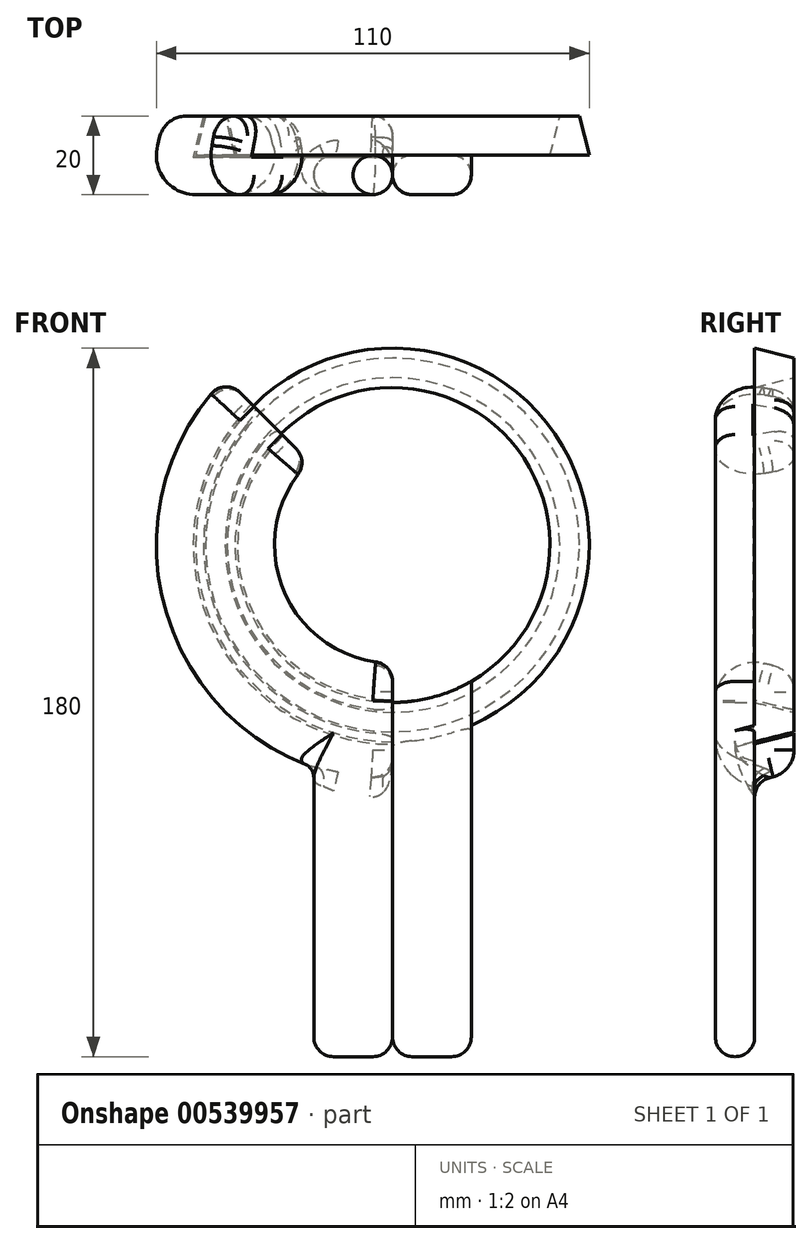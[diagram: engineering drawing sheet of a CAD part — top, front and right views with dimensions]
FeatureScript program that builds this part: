
annotation { "Feature Type Name" : "Feature", "Feature Type Description" : "" }
export const myFeature = defineFeature(function(context is Context, id is Id, definition is map)
    precondition{}
    {
        {
            var Q0;
            Q0=qCreatedBy(makeId("Right.planeOp"),FACE);
            var sketch = newSketch(context, id + "F0", { "sketchPlane" : qUnion([Q0])});
            skLineSegment(sketch, "E0", {"start": v(0, 50) * mm, "end": v(0, 40) * mm});
            skLineSegment(sketch, "E1", {"start": v(0, 40) * mm, "end": v(10, 42.5) * mm});
            skLineSegment(sketch, "E2", {"start": v(10, 42.5) * mm, "end": v(10, 47.5) * mm});
            skLineSegment(sketch, "E3", {"start": v(10, 47.5) * mm, "end": v(0, 50) * mm});
            skPoint(sketch, "E4", {"position": v(0, 45) * mm});
            skPoint(sketch, "E5", {"position": v(10, 45) * mm});
            skLineSegment(sketch, "E6", {"start": v(0, 0) * mm, "end": v(10, 0) * mm});
            skSolve(sketch);
        }
        {
            var Q0;
            Q0 = qSketchRegion(id + "F0", true);
            var Q1;
            Q1=sQuery(id+"F0.wireOp",EDGE,"E6");
            revolve(context, id + "F1", {"entities" : qUnion([Q0]), "axis" : qUnion([Q1]), "revolveType" : RevolveType.FULL});
        }
        {
            var Q0;
            Q0=qCreatedBy(makeId("Front.planeOp"),FACE);
            var sketch = newSketch(context, id + "F2", { "sketchPlane" : qUnion([Q0])});
            skLineSegment(sketch, "E7", {"start": v(0, -40) * mm, "end": v(0, -130) * mm});
            skLineSegment(sketch, "E8", {"start": v(0, -130) * mm, "end": v(20, -130) * mm});
            skLineSegment(sketch, "E9", {"start": v(20, -130) * mm, "end": v(20, -34.64) * mm});
            skArc(sketch, "E10", {"start": v(0, -40) * mm, "mid": v(10.35, -38.64) * mm, "end": v(20, -34.64) * mm});
            skSolve(sketch);
        }
        {
            var Q0;
            Q0 = qSketchRegion(id + "F2", true);
            extrude(context, id + "F3", {"entities" : qUnion([Q0]), "operationType" : NewBodyOperationType.ADD, "depth" : 10 * mm, "offsetDistance" : 25 * mm});
        }
        {
            var Q0;
            Q0=qCreatedBy(makeId("Right.planeOp"),FACE);
            var sketch = newSketch(context, id + "F4", { "sketchPlane" : qUnion([Q0])});
            skLineSegment(sketch, "E11", {"start": v(0, -45) * mm, "end": v(0, -50) * mm});
            skPoint(sketch, "E12", {"position": v(0, -45) * mm});
            skPoint(sketch, "E13", {"position": v(10, -45) * mm});
            skLineSegment(sketch, "E14", {"start": v(0, 0) * mm, "end": v(10, 0) * mm});
            skLineSegment(sketch, "E15.0", {"start": v(-0.5, -50.64) * mm, "end": v(10, -48.02) * mm});
            skLineSegment(sketch, "E15.1", {"start": v(-0.5, -39.36) * mm, "end": v(-0.5, -50.64) * mm});
            skLineSegment(sketch, "E15.2", {"start": v(10, -41.98) * mm, "end": v(-0.5, -39.36) * mm});
            skLineSegment(sketch, "E16.0", {"start": v(-10, -62.8) * mm, "end": v(10, -57.8) * mm});
            skLineSegment(sketch, "E16.1", {"start": v(-10, -27.2) * mm, "end": v(-10, -62.8) * mm});
            skLineSegment(sketch, "E16.2", {"start": v(10, -32.2) * mm, "end": v(-10, -27.2) * mm});
            skLineSegment(sketch, "E17", {"start": v(10, -32.2) * mm, "end": v(10, -41.98) * mm});
            skLineSegment(sketch, "E18", {"start": v(10, -48.02) * mm, "end": v(10, -57.8) * mm});
            skPoint(sketch, "E19.end.orphan", {"position": v(10, -47.5) * mm});
            skPoint(sketch, "E20.start.orphan", {"position": v(10, -42.5) * mm});
            skPoint(sketch, "E21.orphan", {"position": v(0, -40) * mm});
            skSolve(sketch);
        }
        {
            var Q0;
            Q0 = qSketchRegion(id + "F4", true);
            var Q1;
            Q1=sQuery(id+"F0.wireOp",EDGE,"E6");
            revolve(context, id + "F5", {"entities" : qUnion([Q0]), "axis" : qUnion([Q1]), "revolveType" : RevolveType.ONE_DIRECTION, "angle" : 135 * degree});
        }
        {
            var Q0;
            Q0=makeQuery(id+"F5.opRevolve","SWEPT_FACE",FACE,{"disambiguationData":[OSD([sQuery(id+"F4.wireOp",EDGE,"E16.1")])]});
            var sketch = newSketch(context, id + "F6", { "sketchPlane" : qUnion([Q0])});
            skLineSegment(sketch, "E22", {"start": v(0, -130) * mm, "end": v(-20, -130) * mm});
            skLineSegment(sketch, "E23", {"start": v(-20, -130) * mm, "end": v(-20, -54.24) * mm});
            skArc(sketch, "E24", {"start": v(-20, -54.24) * mm, "mid": v(-10.16, -56.9) * mm, "end": v(0, -57.8) * mm});
            skLineSegment(sketch, "E25", {"start": v(0, -57.8) * mm, "end": v(0, -130) * mm});
            skSolve(sketch);
        }
        {
            var Q0;
            Q0 = qSketchRegion(id + "F6", true);
            extrude(context, id + "F7", {"entities" : qUnion([Q0]), "oppositeDirection" : true, "depth" : 10 * mm, "offsetDistance" : 25 * mm});
        }
        {
            var Q0;
            Q0=makeQuery(id+"F5.opRevolve","SWEPT_BODY",BODY,{"disambiguationData":[OSD([sQuery(id+"F4.wireOp",EDGE,"E15.0"),sQuery(id+"F4.wireOp",EDGE,"E15.1"),sQuery(id+"F4.wireOp",EDGE,"E15.2"),sQuery(id+"F4.wireOp",EDGE,"E16.0"),sQuery(id+"F4.wireOp",EDGE,"E16.1"),sQuery(id+"F4.wireOp",EDGE,"E16.2"),sQuery(id+"F4.wireOp",EDGE,"E17"),sQuery(id+"F4.wireOp",EDGE,"E18")])]});
            var Q1;
            Q1=makeQuery(id+"F7.opExtrude","SWEPT_BODY",BODY,{"disambiguationData":[OSD([sQuery(id+"F6.wireOp",EDGE,"E22"),sQuery(id+"F6.wireOp",EDGE,"E23"),sQuery(id+"F6.wireOp",EDGE,"E24"),sQuery(id+"F6.wireOp",EDGE,"E25")])]});
            booleanBodies(context, id + "F8", {"operationType" : BooleanOperationType.UNION, "tools" : qUnion([Q0, Q1])});
        }
        {
            var Q0;
            Q0=makeQuery(id+"F5.opRevolve","SWEPT_EDGE",EDGE,{"disambiguationData":[OSD([sQuery(id+"F4.wireOp",EDGE,"E16.0"),sQuery(id+"F4.wireOp",EDGE,"E18")])]});
            var Q1;
            Q1=makeQuery(id+"F5.opRevolve","SWEPT_EDGE",EDGE,{"disambiguationData":[OSD([sQuery(id+"F4.wireOp",EDGE,"E16.2"),sQuery(id+"F4.wireOp",EDGE,"E17")])]});
            fillet(context, id + "F9", {"entities" : qUnion([Q0, Q1]), "radius" : 7 * mm, "tangentPropagation" : true, "allowEdgeOverflow" : false});
        }
        {
            var Q0;
            Q0=makeQuery(id+"F5.opRevolve","SWEPT_EDGE",EDGE,{"disambiguationData":[OSD([sQuery(id+"F4.wireOp",EDGE,"E16.0"),sQuery(id+"F4.wireOp",EDGE,"E16.1")])]});
            var Q1;
            Q1=makeQuery(id+"F5.opRevolve","SWEPT_EDGE",EDGE,{"disambiguationData":[OSD([sQuery(id+"F4.wireOp",EDGE,"E16.1"),sQuery(id+"F4.wireOp",EDGE,"E16.2")])]});
            var Q2;
            Q2=makeQuery(id+"F3.opExtrude","CAP_EDGE",EDGE,{"disambiguationData":[OSD([sQuery(id+"F2.wireOp",EDGE,"E10")])],"isStart":false});
            var Q3;
            {var subQ0=sQuery(id+"F0.wireOp",EDGE,"E3");Q3=makeQuery(id+"F3.boolean.opBoolean","SPLIT",EDGE,{"disambiguationData":[topologyDisambiguationEdgeConnected([makeQuery(id+"F3.opExtrude","CAP_FACE",FACE,{"disambiguationData":[OSD([sQuery(id+"F2.wireOp",EDGE,"E7"),sQuery(id+"F2.wireOp",EDGE,"E8"),sQuery(id+"F2.wireOp",EDGE,"E9"),sQuery(id+"F2.wireOp",EDGE,"E10")])],"isStart":true})])],"derivedFrom":makeQuery(id+"F1.opRevolve","SWEPT_EDGE",EDGE,{"disambiguationData":[OSD([sQuery(id+"F0.wireOp",EDGE,"E0"),subQ0])]})});}
            fillet(context, id + "F10", {"entities" : qUnion([Q0, Q1, Q2, Q3]), "radius" : 10 * mm, "tangentPropagation" : true, "allowEdgeOverflow" : false});
        }
        {
            var Q0;
            {var subQ0=sQuery(id+"F2.wireOp",EDGE,"E9");Q0=makeQuery(id+"F3.boolean.opBoolean","SPLIT",EDGE,{"disambiguationData":[topologyDisambiguationEdgeConnected([makeQuery(id+"F3.opExtrude","CAP_FACE",FACE,{"disambiguationData":[OSD([sQuery(id+"F2.wireOp",EDGE,"E7"),sQuery(id+"F2.wireOp",EDGE,"E8"),subQ0,sQuery(id+"F2.wireOp",EDGE,"E10")])],"isStart":true})])],"derivedFrom":makeQuery(id+"F3.opExtrude","CAP_EDGE",EDGE,{"disambiguationData":[OSD([subQ0])],"isStart":true})});}
            var Q1;
            Q1=makeQuery(id+"F3.opExtrude","CAP_EDGE",EDGE,{"disambiguationData":[OSD([sQuery(id+"F2.wireOp",EDGE,"E9")])],"isStart":false});
            var Q2;
            Q2=makeQuery(id+"F3.opExtrude","CAP_EDGE",EDGE,{"disambiguationData":[OSD([sQuery(id+"F2.wireOp",EDGE,"E7")])],"isStart":false});
            var Q3;
            Q3=makeQuery(id+"F8.opBoolean","MERGE",EDGE,{"derivedFrom":[makeQuery(id+"F5.opRevolve","CAP_EDGE",EDGE,{"disambiguationData":[OSD([sQuery(id+"F4.wireOp",EDGE,"E16.1")])],"isStart":true}),makeQuery(id+"F7.opExtrude","CAP_EDGE",EDGE,{"disambiguationData":[OSD([sQuery(id+"F6.wireOp",EDGE,"E25")])],"isStart":true})]});
            var Q4;
            Q4=makeQuery(id+"F7.opExtrude","CAP_EDGE",EDGE,{"disambiguationData":[OSD([sQuery(id+"F6.wireOp",EDGE,"E23")])],"isStart":true});
            var Q5;
            Q5=makeQuery(id+"F7.opExtrude","CAP_EDGE",EDGE,{"disambiguationData":[OSD([sQuery(id+"F6.wireOp",EDGE,"E23")])],"isStart":false});
            var Q6;
            Q6=makeQuery(id+"F7.opExtrude","CAP_EDGE",EDGE,{"disambiguationData":[OSD([sQuery(id+"F6.wireOp",EDGE,"E25")])],"isStart":false});
            var Q7;
            {var subQ0=sQuery(id+"F2.wireOp",EDGE,"E7");Q7=makeQuery(id+"F3.boolean.opBoolean","SPLIT",EDGE,{"disambiguationData":[topologyDisambiguationEdgeConnected([makeQuery(id+"F3.opExtrude","CAP_FACE",FACE,{"disambiguationData":[OSD([subQ0,sQuery(id+"F2.wireOp",EDGE,"E8"),sQuery(id+"F2.wireOp",EDGE,"E9"),sQuery(id+"F2.wireOp",EDGE,"E10")])],"isStart":true})])],"derivedFrom":makeQuery(id+"F3.opExtrude","CAP_EDGE",EDGE,{"disambiguationData":[OSD([subQ0])],"isStart":true})});}
            var Q8;
            {var subQ0=sQuery(id+"F4.wireOp",EDGE,"E18");var subQ1=sQuery(id+"F4.wireOp",EDGE,"E16.0");Q8=makeQuery(id+"F9.opFillet","BLEND_EDGE",EDGE,{"blendedFrom":[makeQuery(id+"F5.opRevolve","SWEPT_EDGE",EDGE,{"disambiguationData":[OSD([subQ1,subQ0])]}),makeQuery(id+"F8.opBoolean","MERGE",FACE,{"derivedFrom":[makeQuery(id+"F5.opRevolve","CAP_FACE",FACE,{"disambiguationData":[OSD([sQuery(id+"F4.wireOp",EDGE,"E15.0"),sQuery(id+"F4.wireOp",EDGE,"E15.1"),sQuery(id+"F4.wireOp",EDGE,"E15.2"),subQ1,sQuery(id+"F4.wireOp",EDGE,"E16.1"),sQuery(id+"F4.wireOp",EDGE,"E16.2"),sQuery(id+"F4.wireOp",EDGE,"E17"),subQ0])],"isStart":true}),makeQuery(id+"F7.opExtrude","SWEPT_FACE",FACE,{"disambiguationData":[OSD([sQuery(id+"F6.wireOp",EDGE,"E25")])]})]})],"blendedInto":[makeQuery(id+"F8.opBoolean","MERGE",FACE,{"derivedFrom":[makeQuery(id+"F5.opRevolve","CAP_FACE",FACE,{"disambiguationData":[OSD([sQuery(id+"F4.wireOp",EDGE,"E15.0"),sQuery(id+"F4.wireOp",EDGE,"E15.1"),sQuery(id+"F4.wireOp",EDGE,"E15.2"),subQ1,sQuery(id+"F4.wireOp",EDGE,"E16.1"),sQuery(id+"F4.wireOp",EDGE,"E16.2"),sQuery(id+"F4.wireOp",EDGE,"E17"),subQ0])],"isStart":true}),makeQuery(id+"F7.opExtrude","SWEPT_FACE",FACE,{"disambiguationData":[OSD([sQuery(id+"F6.wireOp",EDGE,"E25")])]})]})]});}
            var Q9;
            {var subQ0=sQuery(id+"F4.wireOp",EDGE,"E16.2");var subQ1=sQuery(id+"F4.wireOp",EDGE,"E16.1");Q9=makeQuery(id+"F10.opFillet","BLEND_EDGE",EDGE,{"blendedFrom":[makeQuery(id+"F5.opRevolve","SWEPT_EDGE",EDGE,{"disambiguationData":[OSD([subQ1,subQ0])]}),makeQuery(id+"F5.opRevolve","CAP_FACE",FACE,{"disambiguationData":[OSD([sQuery(id+"F4.wireOp",EDGE,"E15.0"),sQuery(id+"F4.wireOp",EDGE,"E15.1"),sQuery(id+"F4.wireOp",EDGE,"E15.2"),sQuery(id+"F4.wireOp",EDGE,"E16.0"),subQ1,subQ0,sQuery(id+"F4.wireOp",EDGE,"E17"),sQuery(id+"F4.wireOp",EDGE,"E18")])],"isStart":false})],"blendedInto":[makeQuery(id+"F5.opRevolve","CAP_FACE",FACE,{"disambiguationData":[OSD([sQuery(id+"F4.wireOp",EDGE,"E15.0"),sQuery(id+"F4.wireOp",EDGE,"E15.1"),sQuery(id+"F4.wireOp",EDGE,"E15.2"),sQuery(id+"F4.wireOp",EDGE,"E16.0"),subQ1,subQ0,sQuery(id+"F4.wireOp",EDGE,"E17"),sQuery(id+"F4.wireOp",EDGE,"E18")])],"isStart":false})]});}
            var Q10;
            Q10=makeQuery(id+"F7.opExtrude","CAP_EDGE",EDGE,{"disambiguationData":[OSD([sQuery(id+"F6.wireOp",EDGE,"E22")])],"isStart":true});
            var Q11;
            Q11=makeQuery(id+"F3.opExtrude","CAP_EDGE",EDGE,{"disambiguationData":[OSD([sQuery(id+"F2.wireOp",EDGE,"E8")])],"isStart":false});
            var Q12;
            Q12=makeQuery(id+"F3.opExtrude","SWEPT_EDGE",EDGE,{"disambiguationData":[OSD([sQuery(id+"F2.wireOp",EDGE,"E8"),sQuery(id+"F2.wireOp",EDGE,"E9")])]});
            var Q13;
            Q13=makeQuery(id+"F3.opExtrude","SWEPT_FACE",FACE,{"disambiguationData":[OSD([sQuery(id+"F2.wireOp",EDGE,"E8")])]});
            var Q14;
            Q14=makeQuery(id+"F7.opExtrude","SWEPT_EDGE",EDGE,{"disambiguationData":[OSD([sQuery(id+"F6.wireOp",EDGE,"E22"),sQuery(id+"F6.wireOp",EDGE,"E23")])]});
            var Q15;
            Q15=makeQuery(id+"F3.opExtrude","SWEPT_EDGE",EDGE,{"disambiguationData":[OSD([sQuery(id+"F2.wireOp",EDGE,"E7"),sQuery(id+"F2.wireOp",EDGE,"E8")])]});
            var Q16;
            Q16=makeQuery(id+"F7.opExtrude","SWEPT_EDGE",EDGE,{"disambiguationData":[OSD([sQuery(id+"F6.wireOp",EDGE,"E22"),sQuery(id+"F6.wireOp",EDGE,"E25")])]});
            var Q17;
            Q17=makeQuery(id+"F7.opExtrude","CAP_EDGE",EDGE,{"disambiguationData":[OSD([sQuery(id+"F6.wireOp",EDGE,"E22")])],"isStart":false});
            fillet(context, id + "F11", {"entities" : qUnion([Q0, Q1, Q2, Q3, Q4, Q5, Q6, Q7, Q8, Q9, Q10, Q11, Q12, Q13, Q14, Q15, Q16, Q17]), "radius" : 5 * mm, "tangentPropagation" : true, "allowEdgeOverflow" : false});
        }
        {
            var Q0;
            Q0=makeQuery(id+"F10.opFillet","BLEND_EDGE",EDGE,{"blendedFrom":[makeQuery(id+"F5.opRevolve","SWEPT_EDGE",EDGE,{"disambiguationData":[OSD([sQuery(id+"F4.wireOp",EDGE,"E16.0"),sQuery(id+"F4.wireOp",EDGE,"E16.1")])]}),makeQuery(id+"F7.opExtrude","CAP_FACE",FACE,{"disambiguationData":[OSD([sQuery(id+"F6.wireOp",EDGE,"E22"),sQuery(id+"F6.wireOp",EDGE,"E23"),sQuery(id+"F6.wireOp",EDGE,"E24"),sQuery(id+"F6.wireOp",EDGE,"E25")])],"isStart":false})],"blendedInto":[makeQuery(id+"F7.opExtrude","CAP_FACE",FACE,{"disambiguationData":[OSD([sQuery(id+"F6.wireOp",EDGE,"E22"),sQuery(id+"F6.wireOp",EDGE,"E23"),sQuery(id+"F6.wireOp",EDGE,"E24"),sQuery(id+"F6.wireOp",EDGE,"E25")])],"isStart":false})]});
            fillet(context, id + "F12", {"entities" : qUnion([Q0]), "radius" : 5 * mm, "tangentPropagation" : true, "allowEdgeOverflow" : false});
        }
    });
